# Revit family: HERZ Strömax Балансировочный клапан с измерительными клапанами, шпиндель наклонный 4220 GF PN25
name_source: partatom
category: Rohrzubehör
units: mm (PartAtom-declared; Revit-internal decimal feet)

## family parameters
Arbeitsebenenbasiert = Nein
Beim Laden mit Abzugskörper schneiden = Nein
Bemaßung runder Anschluss = Durchmesser verwenden
Gemeinsam genutzt = Nein
Immer vertikal = Ja
OmniClass-Nummer = 23.65.55.14
OmniClass-Titel = Valves for Liquid Services
Teiletyp = Unterbricht

## types (1)
- HERZ Strömax Балансировочный клапан с измерительными клапанами, шпиндель наклонный 4220 GF PN25
    D05 = 75 mm  [stored 0.246063 ft]
    GT = 10 mm  [stored 0.0328084 ft]
    H06 = 27 mm  [stored 0.0885827 ft]
    H07 = 50 mm  [stored 0.164042 ft]
    H08 = 47 mm  [stored 0.154199 ft]
    H11 = 85 mm  [stored 0.278871 ft]
    Hersteller = HERZ Armaturen Ges.m.b.H.
    O-Ring = EPDM
    SCRNCODE = 05;07;02
    SCRNSEQ = ARM;ARM_TYP="STRV";2
    URL = www.herz-armaturen.ru
    Vorgabe-Ansicht = 0 mm  [stored 0 ft]
    W01 = 50.00°
    W02 = 60.00°
    Букса = чугун с шаровидным графитом EN-GJS-400-15
    Измерение перепада давления = Балансировочный клапан STRÖMAX GF оборудован двумя измерительными клапанами:
при использовании соответствующего измерительного прибора можно измерить перепад давления и благодаря этому можно соответственно определить расход.
    Исполнение = Балансировочный клапан STRÖMAX-GF с измерительными клапанами, DN 350-500, корпус из чугуна с шаровидным графитом GJS 400-15 в соответствии с EN 1561, фланцы в соответствии с EN 1092, PN 16 или PN 25, покрыт синей эмалью.
Букса из чугуна с шаровидным графитом GJS 400-15, с неподнимающимся шпинделем, уплотнение шпинделя с посощью тройных кольцевых уплотнений.
Цифровой лимб указателя настройки.
    Кегель клапана = чугун с шаровидным графитом EN-GJS-400-15 согласно EN 1561 / EPDM с покрытием
    Корпус = чугун с шаровидным графитом EN-GJS-400-15
    Макс. рабочая температура = 110 °C
    Макс. рабочее давление = 2500000.0 Pa
    Мин. рабочая температура = -10 °C
    Область применения = Для гидравлической балансировки в системах отопления или охлаждения, регулирования и перекрытия трубопроводов, стояков, теплообменников, тепловых и холодильных регистров.
    Регулирующий шпиндель = нержавеющая сталь
    Среда = Допускается использование этилен- и пропиленгликоля в концентрации смеси 25-50% объема.
Качество теплоносителя согласно ÖNORM H 5195 и VDI 2035.
    Счетное устройство = пластмасса
    Шпиндель = нержавеющая сталь

note: [stored X ft] marks values corroborated as IEEE doubles in the binary element streams (Revit-internal decimal feet)
